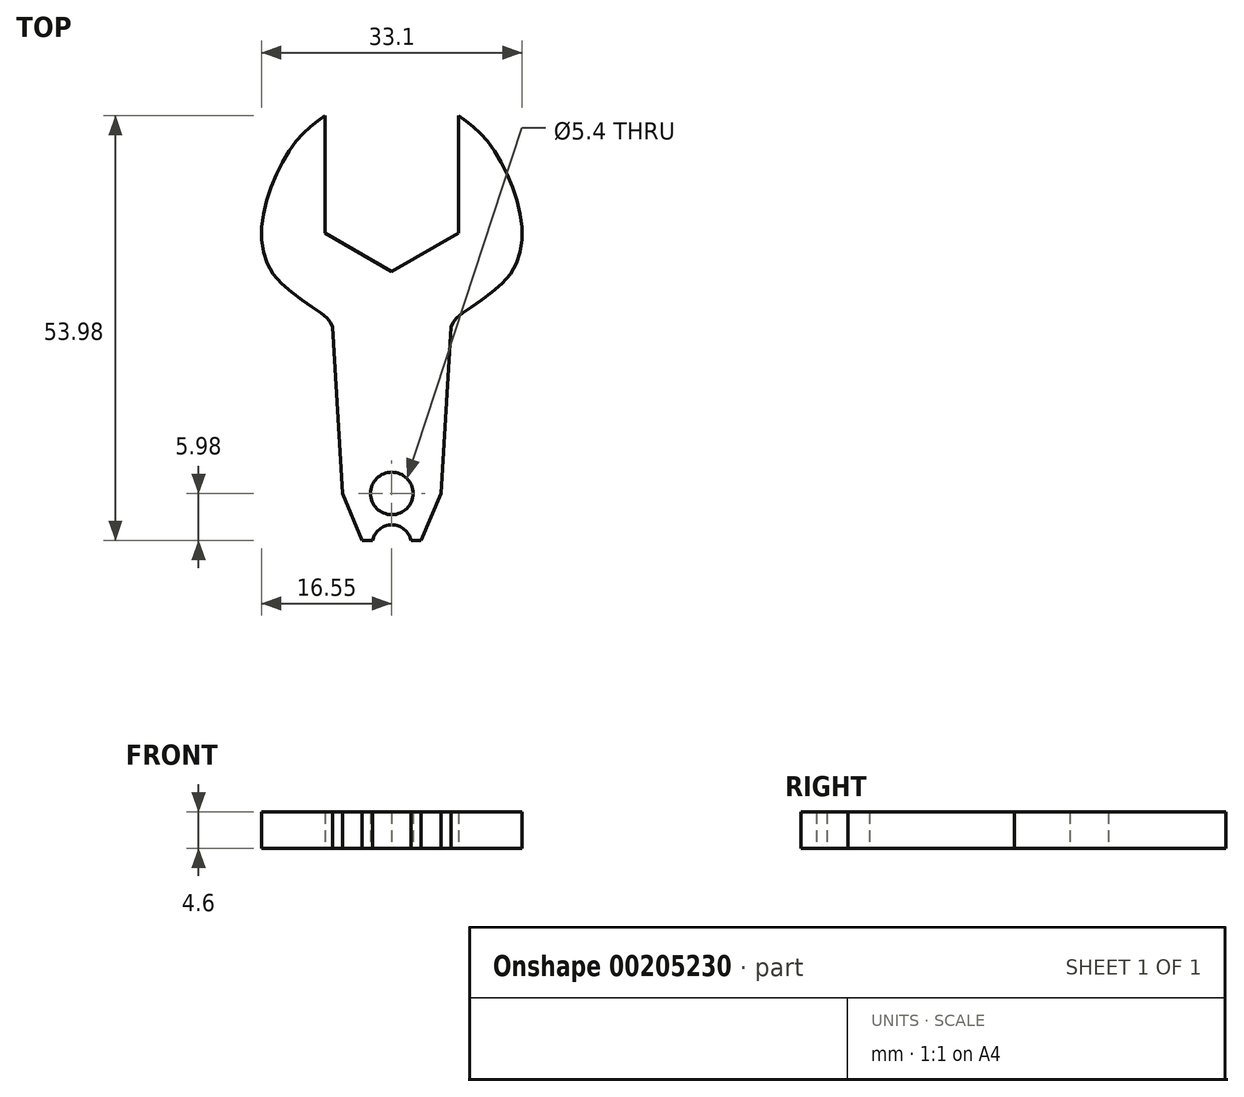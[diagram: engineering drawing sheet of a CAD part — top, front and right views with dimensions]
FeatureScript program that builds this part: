
annotation { "Feature Type Name" : "Feature", "Feature Type Description" : "" }
export const myFeature = defineFeature(function(context is Context, id is Id, definition is map)
    precondition{}
    {
        {
            var Q0;
            Q0=qCreatedBy(makeId("Top.planeOp"),FACE);
            var sketch = newSketch(context, id + "F0", { "sketchPlane" : qUnion([Q0])});
            skCircle(sketch, "E0", {"center": v(0, 0) * mm, "radius": 2.5 * mm});
            skLineSegment(sketch, "E1", {"start": v(0, -2.5) * mm, "end": v(0, -4) * mm});
            skLineSegment(sketch, "E2", {"start": v(0, -4) * mm, "end": v(0, -6.5) * mm});
            skCircle(sketch, "E3", {"center": v(0, -6.5) * mm, "radius": 2.5 * mm});
            skLineSegment(sketch, "E4", {"start": v(2.5, 0) * mm, "end": v(6.25, 0) * mm});
            skLineSegment(sketch, "E5", {"start": v(-2.5, 0) * mm, "end": v(-6.25, 0) * mm});
            skLineSegment(sketch, "E6", {"start": v(0, -4) * mm, "end": v(0, -5.98) * mm});
            skLineSegment(sketch, "E7", {"start": v(0, -5.98) * mm, "end": v(-4.02, -5.98) * mm});
            skLineSegment(sketch, "E8", {"start": v(0, -5.98) * mm, "end": v(2.28, -5.98) * mm});
            skLineSegment(sketch, "E9", {"start": v(0, -5.98) * mm, "end": v(5, -5.98) * mm});
            skLineSegment(sketch, "E10", {"start": v(0, -5.98) * mm, "end": v(-5, -5.98) * mm});
            skLineSegment(sketch, "E11", {"start": v(5, -5.98) * mm, "end": v(2.5, -5.98) * mm});
            skLineSegment(sketch, "E12", {"start": v(-2.5, -5.98) * mm, "end": v(-5, -5.98) * mm});
            skLineSegment(sketch, "E13", {"start": v(-6.25, 0) * mm, "end": v(-3.75, -5.98) * mm});
            skLineSegment(sketch, "E14", {"start": v(6.25, 0) * mm, "end": v(3.75, -5.98) * mm});
            skLineSegment(sketch, "E15", {"start": v(0, 2.5) * mm, "end": v(0, 29.5) * mm});
            skLineSegment(sketch, "E16", {"start": v(0, 29.5) * mm, "end": v(0, 38) * mm});
            skCircle(sketch, "E17", {"center": v(0, 38) * mm, "radius": 8.5 * mm});
            skLineSegment(sketch, "E18", {"start": v(0, 38) * mm, "end": v(-8.5, 38) * mm});
            skLineSegment(sketch, "E19", {"start": v(-8.5, 38) * mm, "end": v(-6.25, 0) * mm});
            skLineSegment(sketch, "E20", {"start": v(8.5, 38) * mm, "end": v(6.25, 0) * mm});
            skLineSegment(sketch, "E21", {"start": v(-8.5, 38) * mm, "end": v(-8.5, 48) * mm});
            skLineSegment(sketch, "E22", {"start": v(-8.5, 48) * mm, "end": v(8.5, 48) * mm});
            skLineSegment(sketch, "E23", {"start": v(8.5, 48) * mm, "end": v(8.5, 38) * mm});
            skFitSpline(sketch, "E24", {"points": [v(-8.5, 48) * mm, v(-12.37, 44.45) * mm, v(-16.33, 35.35) * mm, v(-14.7, 27.42) * mm, v(-8.5, 22.52) * mm, v(-7.5, 21.16) * mm], "startDerivative": vector(-21.14, -15.5) * mm, "endDerivative": vector(5.74, -12.02) * mm});
            skFitSpline(sketch, "E25.MirrorCS", {"points": [v(8.5, 48) * mm, v(12.37, 44.45) * mm, v(16.33, 35.35) * mm, v(14.7, 27.42) * mm, v(8.5, 22.52) * mm, v(7.5, 21.16) * mm], "startDerivative": vector(21.14, -15.5) * mm, "endDerivative": vector(-5.74, -12.02) * mm});
            skCircle(sketch, "E26.cCircle", {"center": v(0, 38) * mm, "radius": 8.5 * mm, "construction": true});
            skLineSegment(sketch, "E26.0", {"start": v(8.5, 42.9) * mm, "end": v(8.5, 33.1) * mm});
            skLineSegment(sketch, "E26.1", {"start": v(8.5, 33.1) * mm, "end": v(0, 28.19) * mm});
            skLineSegment(sketch, "E26.2", {"start": v(0, 28.19) * mm, "end": v(-8.5, 33.1) * mm});
            skLineSegment(sketch, "E26.3", {"start": v(-8.5, 33.1) * mm, "end": v(-8.5, 42.9) * mm});
            skLineSegment(sketch, "E26.4", {"start": v(-8.5, 42.9) * mm, "end": v(0, 47.81) * mm});
            skLineSegment(sketch, "E26.5", {"start": v(0, 47.81) * mm, "end": v(8.5, 42.9) * mm});
            skPoint(sketch, "E26.0.midPoint", {"position": v(8.5, 38) * mm});
            skCircle(sketch, "E27", {"center": v(0, 0) * mm, "radius": 2.7 * mm});
            skSolve(sketch);
        }
        {
            var Q0;
            {var subQ0=sQuery(id+"F0.wireOp",EDGE,"E21");Q0=makeQuery(id+"F0.imprint","IMPRINT",FACE,{"disambiguationData":[TD([[makeQuery(id+"F0.imprint","IMPRINT",EDGE,{"derivedFrom":subQ0}),1.0]])]});}
            var Q1;
            {var subQ0=sQuery(id+"F0.wireOp",EDGE,"E23");Q1=makeQuery(id+"F0.imprint","IMPRINT",FACE,{"disambiguationData":[TD([[makeQuery(id+"F0.imprint","IMPRINT",EDGE,{"derivedFrom":subQ0}),1.0]])]});}
            var Q2;
            {var subQ0=sQuery(id+"F0.wireOp",EDGE,"E20");var subQ3=makeQuery(id+"F0.imprint","INTERSECT",VERTEX,{"derivedFrom":[subQ0,sQuery(id+"F0.wireOp",EDGE,"E25.MirrorCS")]});Q2=makeQuery(id+"F0.imprint","IMPRINT",FACE,{"disambiguationData":[TD([[makeQuery(id+"F0.imprint","IMPRINT",EDGE,{"disambiguationData":[TD([[subQ3,1.0]])],"derivedFrom":subQ0}),-1.0]])]});}
            var Q3;
            {var subQ0=sQuery(id+"F0.wireOp",EDGE,"E19");var subQ3=makeQuery(id+"F0.imprint","INTERSECT",VERTEX,{"derivedFrom":[subQ0,sQuery(id+"F0.wireOp",EDGE,"E24")]});Q3=makeQuery(id+"F0.imprint","IMPRINT",FACE,{"disambiguationData":[TD([[makeQuery(id+"F0.imprint","IMPRINT",EDGE,{"disambiguationData":[TD([[subQ3,1.0]])],"derivedFrom":subQ0}),1.0]])]});}
            var Q4;
            {var subQ0=sQuery(id+"F0.wireOp",EDGE,"E14");Q4=makeQuery(id+"F0.imprint","IMPRINT",FACE,{"disambiguationData":[TD([[makeQuery(id+"F0.imprint","IMPRINT",EDGE,{"derivedFrom":subQ0}),-1.0]])]});}
            var Q5;
            {var subQ0=sQuery(id+"F0.wireOp",EDGE,"E13");Q5=makeQuery(id+"F0.imprint","IMPRINT",FACE,{"disambiguationData":[TD([[makeQuery(id+"F0.imprint","IMPRINT",EDGE,{"derivedFrom":subQ0}),1.0]])]});}
            extrude(context, id + "F1", {"entities" : qUnion([Q0, Q1, Q2, Q3, Q4, Q5]), "depth" : 4.6 * mm});
        }
    });
